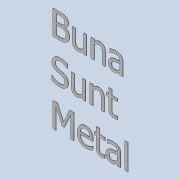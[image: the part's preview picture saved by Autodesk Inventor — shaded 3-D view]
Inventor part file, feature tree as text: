
AUTODESK INVENTOR PART (.ipt)
format: ipt  version: 2020 (Build 240168000, 168)  size: 420,352 bytes
history: native  units: mm
features: extrude x1, sketch x1
ambient origin geometry x8: Origin, YZ Plane, XZ Plane, XY Plane, X Axis, Y Axis, Z Axis, Center Point
bodies: Solid1 (feature_tree)
feature tree (2):
  extrude  "Extrusion1"  Depth=420.0mm
  sketch  "Sketch1"  dims[d0=297.0mm d1=420.0mm d2=0.8mm d3=0.0mm]
